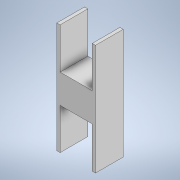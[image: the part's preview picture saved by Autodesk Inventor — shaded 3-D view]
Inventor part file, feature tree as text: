
AUTODESK INVENTOR PART (.ipt)
format: ipt  version: 2020 (Build 240168000, 168)  size: 130,560 bytes
history: native  units: mm
features: extrude x2, sketch x1
ambient origin geometry x8: Origin, YZ Plane, XZ Plane, XY Plane, X Axis, Y Axis, Z Axis, Center Point
bodies: Solid1 (feature_tree)
feature tree (3):
  extrude  "Extrusion1"  Depth=80.0mm
  extrude  "Extrusion2"  Depth=80.0mm
  sketch  "Sketch2"  dims[d0=70.0mm d1=80.0mm d2=80.0mm d3=6.0mm d4=50.0mm d5=0.0mm d7=6.0mm d8=40.0mm d9=0.0mm d10=20.0mm d6=0.5mm]
